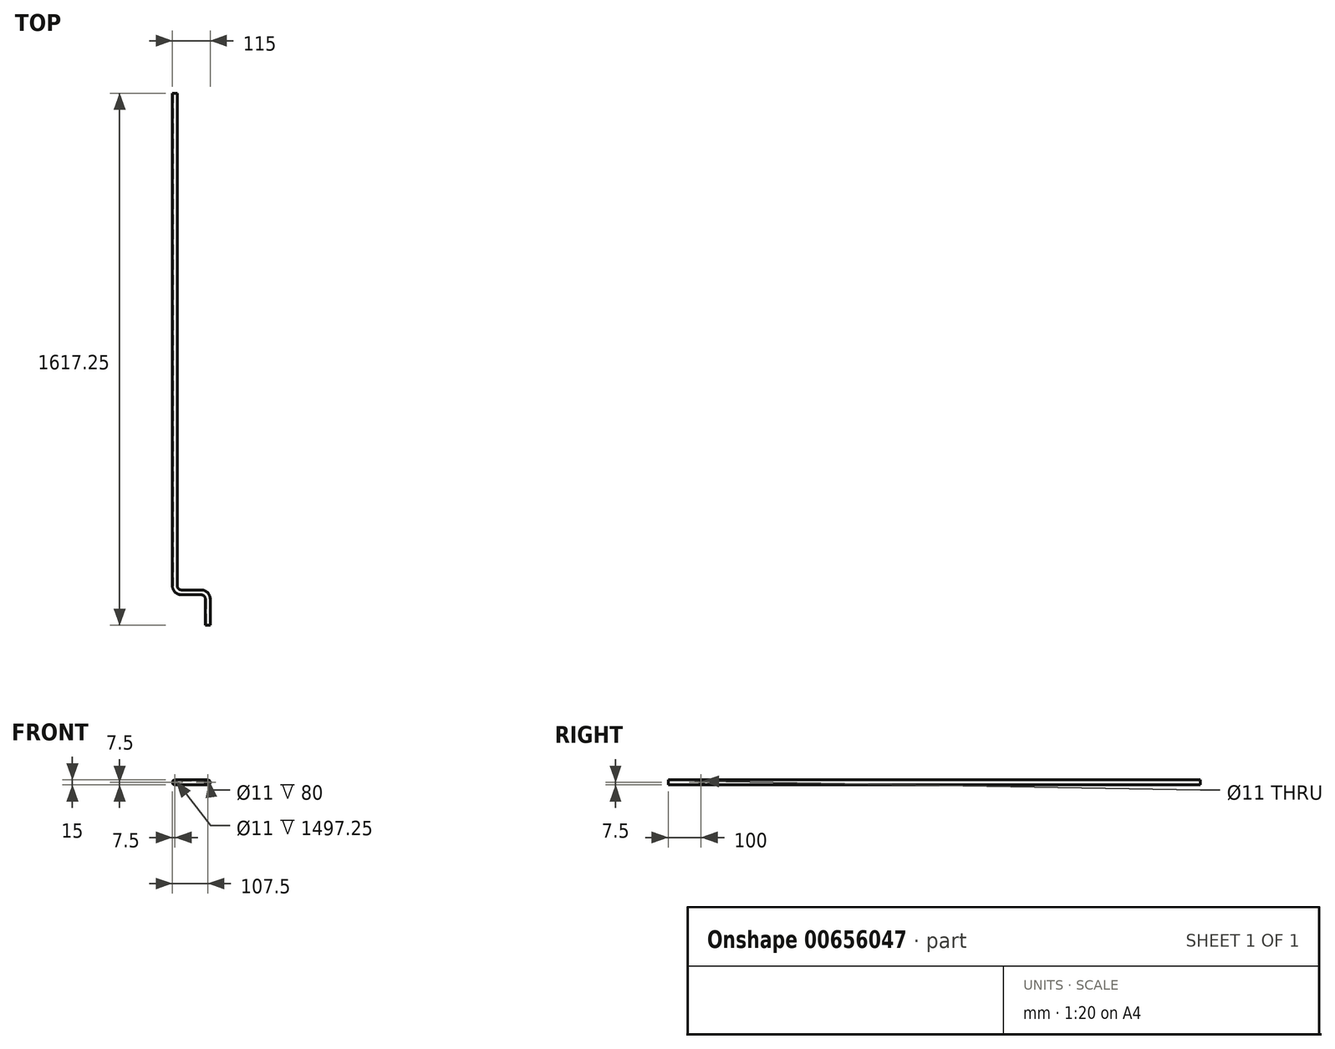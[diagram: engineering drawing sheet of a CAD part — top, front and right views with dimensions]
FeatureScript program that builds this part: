
annotation { "Feature Type Name" : "Feature", "Feature Type Description" : "" }
export const myFeature = defineFeature(function(context is Context, id is Id, definition is map)
    precondition{}
    {
        {
            var Q0;
            Q0=qCreatedBy(makeId("Front.planeOp"),FACE);
            var sketch = newSketch(context, id + "F0", { "sketchPlane" : qUnion([Q0])});
            skCircle(sketch, "E0", {"center": v(0, 0) * mm, "radius": 7.5 * mm});
            skCircle(sketch, "E1.0", {"center": v(0, 0) * mm, "radius": 5.5 * mm});
            skSolve(sketch);
        }
        {
            var Q0;
            Q0=qCreatedBy(makeId("Top.planeOp"),FACE);
            var sketch = newSketch(context, id + "F1", { "sketchPlane" : qUnion([Q0])});
            skLineSegment(sketch, "E2", {"start": v(0, 0) * mm, "end": v(0, -1480) * mm});
            skLineSegment(sketch, "E3", {"start": v(20, -1500) * mm, "end": v(80, -1500) * mm});
            skLineSegment(sketch, "E4", {"start": v(100, -1520) * mm, "end": v(100, -1600) * mm});
            skPoint(sketch, "E5.visualSharp", {"position": v(0, -1500) * mm});
            skArc(sketch, "E5.filletArc", {"start": v(0, -1480) * mm, "mid": v(5.86, -1494.14) * mm, "end": v(20, -1500) * mm});
            skPoint(sketch, "E6.visualSharp", {"position": v(100, -1500) * mm});
            skArc(sketch, "E6.filletArc", {"start": v(100, -1520) * mm, "mid": v(94.14, -1505.86) * mm, "end": v(80, -1500) * mm});
            skSolve(sketch);
        }
        {
            var Q0;
            Q0=makeQuery(id+"F0.imprint","IMPRINT",FACE,{"disambiguationData":[TD([[makeQuery(id+"F0.imprint","IMPRINT",EDGE,{"derivedFrom":sQuery(id+"F0.wireOp",EDGE,"E0")}),1.0]])]});
            var Q1;
            Q1=sQuery(id+"F1.wireOp",EDGE,"E2");
            var Q2;
            Q2=sQuery(id+"F1.wireOp",EDGE,"E5.filletArc");
            var Q3;
            Q3=sQuery(id+"F1.wireOp",EDGE,"E3");
            var Q4;
            Q4=sQuery(id+"F1.wireOp",EDGE,"E6.filletArc");
            var Q5;
            Q5=sQuery(id+"F1.wireOp",EDGE,"E4");
            sweep(context, id + "F2", {"profiles" : qUnion([Q0]), "path" : qUnion([Q1, Q2, Q3, Q4, Q5])});
        }
        {
            var Q0;
            Q0=makeQuery(id+"F2.opSweep","CAP_FACE",FACE,{"disambiguationData":[OSD([sQuery(id+"F0.wireOp",EDGE,"E0"),sQuery(id+"F0.wireOp",EDGE,"E1.0"),sQuery(id+"F1.wireOp",VERTEX,"E2.start")])],"isStart":true});
            extrude(context, id + "F3", {"entities" : qUnion([Q0]), "operationType" : NewBodyOperationType.ADD, "depth" : 17.25 * mm, "offsetDistance" : 25.4 * mm});
        }
    });
